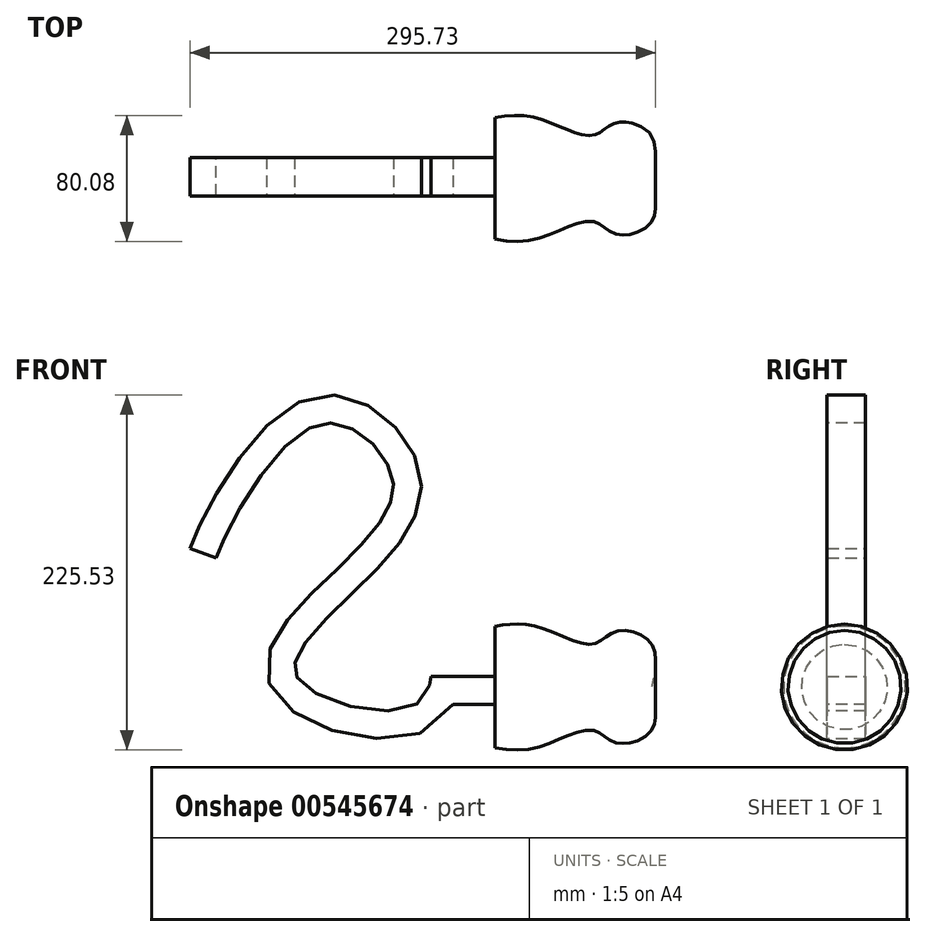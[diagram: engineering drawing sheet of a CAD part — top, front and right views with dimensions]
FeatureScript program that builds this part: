
annotation { "Feature Type Name" : "Feature", "Feature Type Description" : "" }
export const myFeature = defineFeature(function(context is Context, id is Id, definition is map)
    precondition{}
    {
        {
            var Q0;
            Q0=qCreatedBy(makeId("Front.planeOp"),FACE);
            var sketch = newSketch(context, id + "F0", { "sketchPlane" : qUnion([Q0])});
            skLineSegment(sketch, "E0", {"start": v(0, 0) * mm, "end": v(-34.87, 0) * mm});
            skFitSpline(sketch, "E1", {"points": [v(-34.87, 0) * mm, v(-129.65, 0) * mm, v(-95.82, 64.01) * mm, v(-54.4, 134.8) * mm, v(-115.8, 177.2) * mm, v(-187.43, 85.64) * mm], "startDerivative": vector(-80.88, -524.38) * mm, "endDerivative": vector(-79.14, -221.75) * mm});
            skSolve(sketch);
        }
        {
            var Q0;
            Q0=qCreatedBy(makeId("Front.planeOp"),FACE);
            var sketch = newSketch(context, id + "F1", { "sketchPlane" : qUnion([Q0])});
            skFitSpline(sketch, "E2", {"points": [v(0, 38.63) * mm, v(26.8, 38.34) * mm, v(61.67, 27.29) * mm, v(76.41, 35.22) * mm, v(98.8, 28.14) * mm, v(99.38, 0) * mm], "startDerivative": vector(122.66, 18.79) * mm, "endDerivative": vector(-32.63, -153.68) * mm});
            skLineSegment(sketch, "E3", {"start": v(99.38, 0) * mm, "end": v(0, 0) * mm});
            skLineSegment(sketch, "E4", {"start": v(0, 0) * mm, "end": v(0, 38.63) * mm});
            skSolve(sketch);
        }
        {
            var Q0;
            Q0=qCreatedBy(makeId("Right.planeOp"),FACE);
            var sketch = newSketch(context, id + "F2", { "sketchPlane" : qUnion([Q0])});
            skLineSegment(sketch, "E5.bottom", {"start": v(-11.02, 6.8) * mm, "end": v(13.41, 6.8) * mm});
            skLineSegment(sketch, "E5.top", {"start": v(-11.02, -10.92) * mm, "end": v(13.41, -10.92) * mm});
            skLineSegment(sketch, "E5.left", {"start": v(-11.02, 6.8) * mm, "end": v(-11.02, -10.92) * mm});
            skLineSegment(sketch, "E5.right", {"start": v(13.41, 6.8) * mm, "end": v(13.41, -10.92) * mm});
            skSolve(sketch);
        }
        {
            var Q0;
            Q0=makeQuery(id+"F2.imprint","IMPRINT",FACE,{"disambiguationData":[TD([[makeQuery(id+"F2.imprint","IMPRINT",EDGE,{"derivedFrom":sQuery(id+"F2.wireOp",EDGE,"E5.bottom")}),-1.0]])]});
            var Q1;
            Q1=sQuery(id+"F0.wireOp",EDGE,"E1");
            var Q2;
            Q2=sQuery(id+"F0.wireOp",EDGE,"E0");
            sweep(context, id + "F3", {"profiles" : qUnion([Q0]), "path" : qUnion([Q1, Q2])});
        }
        {
            var Q0;
            Q0=makeQuery(id+"F1.imprint","IMPRINT",FACE,{"disambiguationData":[TD([[makeQuery(id+"F1.imprint","IMPRINT",EDGE,{"derivedFrom":sQuery(id+"F1.wireOp",EDGE,"E2")}),-1.0]])]});
            var Q1;
            Q1=sQuery(id+"F1.wireOp",EDGE,"E3");
            revolve(context, id + "F4", {"operationType" : NewBodyOperationType.ADD, "entities" : qUnion([Q0]), "axis" : qUnion([Q1]), "revolveType" : RevolveType.FULL});
        }
    });
